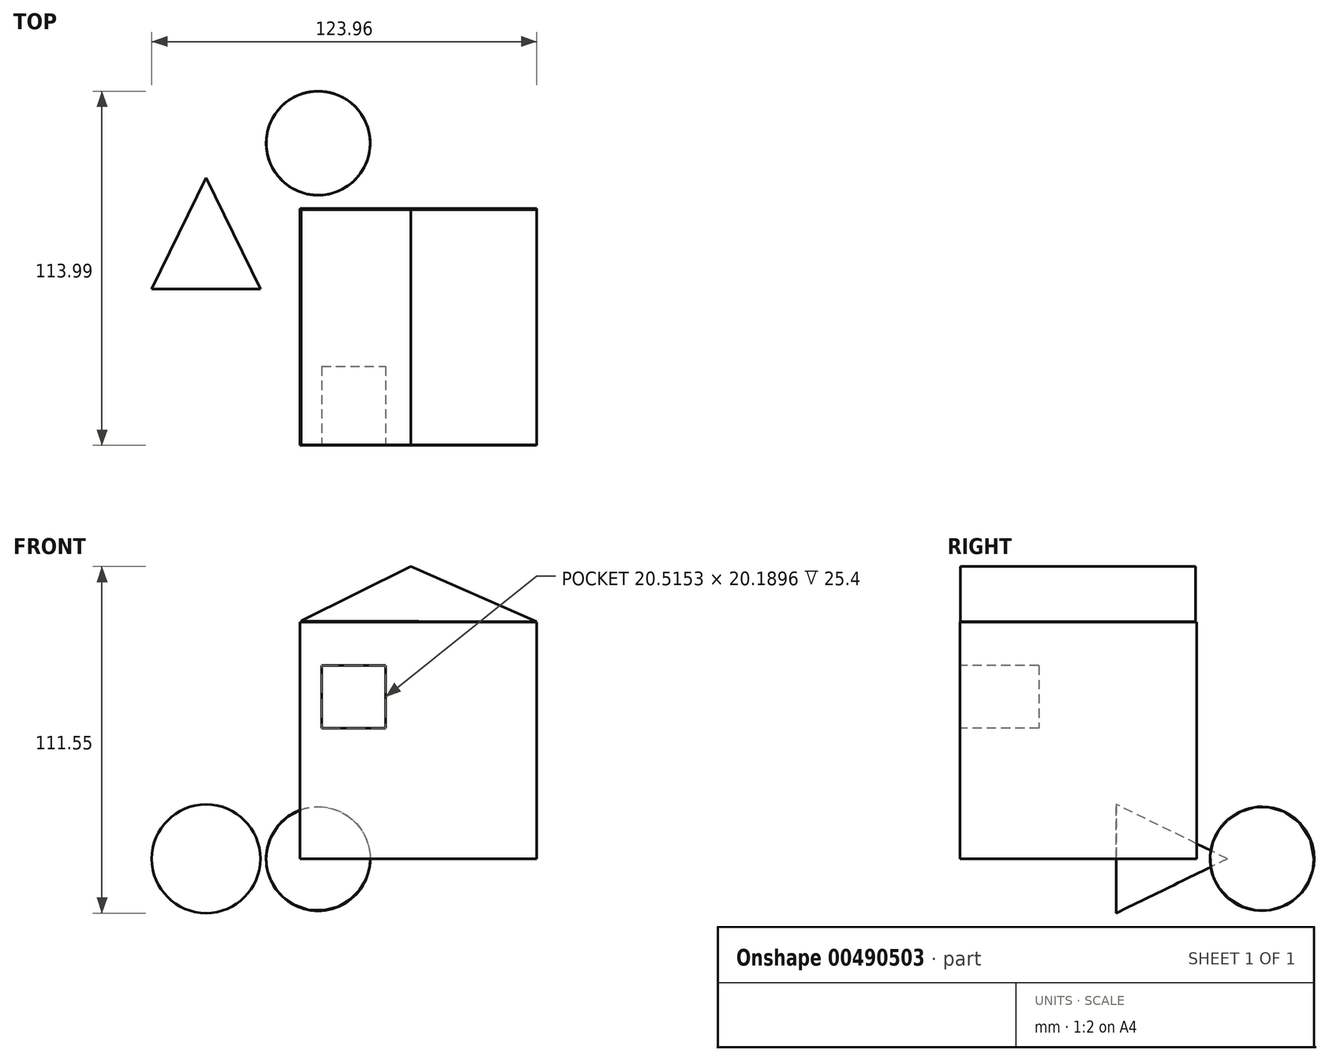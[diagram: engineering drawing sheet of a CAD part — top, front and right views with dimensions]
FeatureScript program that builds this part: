
annotation { "Feature Type Name" : "Feature", "Feature Type Description" : "" }
export const myFeature = defineFeature(function(context is Context, id is Id, definition is map)
    precondition{}
    {
        {
            var Q0;
            Q0=qCreatedBy(makeId("Top.planeOp"),FACE);
            var sketch = newSketch(context, id + "F0", { "sketchPlane" : qUnion([Q0])});
            skLineSegment(sketch, "E0.bottom", {"start": v(-35.62, 39.46) * mm, "end": v(40.58, 39.46) * mm});
            skLineSegment(sketch, "E0.top", {"start": v(-35.62, -36.74) * mm, "end": v(40.58, -36.74) * mm});
            skLineSegment(sketch, "E0.left", {"start": v(-35.62, 39.46) * mm, "end": v(-35.62, -36.74) * mm});
            skLineSegment(sketch, "E0.right", {"start": v(40.58, 39.46) * mm, "end": v(40.58, -36.74) * mm});
            skSolve(sketch);
        }
        {
            var Q0;
            Q0 = qSketchRegion(id + "F0", true);
            extrude(context, id + "F1", {"entities" : qUnion([Q0]), "depth" : 76.2 * mm});
        }
        {
            var Q0;
            Q0=qCreatedBy(makeId("Front.planeOp"),FACE);
            var sketch = newSketch(context, id + "F2", { "sketchPlane" : qUnion([Q0])});
            skLineSegment(sketch, "E1", {"start": v(-35.27, 76.57) * mm, "end": v(0, 94.06) * mm});
            skLineSegment(sketch, "E2", {"start": v(0, 94.06) * mm, "end": v(40.52, 76.28) * mm});
            skLineSegment(sketch, "E3", {"start": v(40.52, 76.28) * mm, "end": v(-35.27, 76.57) * mm});
            skSolve(sketch);
        }
        {
            var Q0;
            Q0=makeQuery(id+"F2.imprint","IMPRINT",FACE,{"disambiguationData":[TD([[makeQuery(id+"F2.imprint","IMPRINT",EDGE,{"derivedFrom":sQuery(id+"F2.wireOp",EDGE,"E1")}),-1.0]])]});
            extrude(context, id + "F3", {"entities" : qUnion([Q0]), "depth" : 36.58 * mm, "hasSecondDirection" : true, "secondDirectionOppositeDirection" : true, "secondDirectionDepth" : 39.12 * mm});
        }
        {
            var Q0;
            Q0=makeQuery(id+"F1.opExtrude","SWEPT_FACE",FACE,{"disambiguationData":[OSD([sQuery(id+"F0.wireOp",EDGE,"E0.top")])]});
            var sketch = newSketch(context, id + "F4", { "sketchPlane" : qUnion([Q0])});
            skLineSegment(sketch, "E4.bottom", {"start": v(-28.66, 62.17) * mm, "end": v(-8.14, 62.17) * mm});
            skLineSegment(sketch, "E4.top", {"start": v(-28.66, 41.98) * mm, "end": v(-8.14, 41.98) * mm});
            skLineSegment(sketch, "E4.left", {"start": v(-28.66, 62.17) * mm, "end": v(-28.66, 41.98) * mm});
            skLineSegment(sketch, "E4.right", {"start": v(-8.14, 62.17) * mm, "end": v(-8.14, 41.98) * mm});
            skSolve(sketch);
        }
        {
            var Q0;
            Q0 = qSketchRegion(id + "F4", true);
            extrude(context, id + "F5", {"entities" : qUnion([Q0]), "operationType" : NewBodyOperationType.REMOVE, "oppositeDirection" : true, "depth" : 25.4 * mm});
        }
        {
            var Q0;
            Q0=qCreatedBy(makeId("Top.planeOp"),FACE);
            var sketch = newSketch(context, id + "F6", { "sketchPlane" : qUnion([Q0])});
            skLineSegment(sketch, "E5", {"start": v(-65.9, 49.4) * mm, "end": v(-65.9, 13.55) * mm});
            skLineSegment(sketch, "E6", {"start": v(-65.9, 13.55) * mm, "end": v(-48.4, 13.55) * mm});
            skLineSegment(sketch, "E7", {"start": v(-48.4, 13.55) * mm, "end": v(-65.9, 49.4) * mm});
            skSolve(sketch);
        }
        {
            var Q0;
            Q0=makeQuery(id+"F6.imprint","IMPRINT",FACE,{"disambiguationData":[TD([[makeQuery(id+"F6.imprint","IMPRINT",EDGE,{"derivedFrom":sQuery(id+"F6.wireOp",EDGE,"E5")}),1.0]])]});
            var Q1;
            Q1=sQuery(id+"F6.wireOp",EDGE,"E5");
            revolve(context, id + "F7", {"entities" : qUnion([Q0]), "axis" : qUnion([Q1]), "revolveType" : RevolveType.ONE_DIRECTION, "oppositeDirection" : true, "angle" : 360 * degree});
        }
        {
            var Q0;
            Q0=qCreatedBy(makeId("Top.planeOp"),FACE);
            var sketch = newSketch(context, id + "F8", { "sketchPlane" : qUnion([Q0])});
            skCircle(sketch, "E8", {"center": v(-29.82, 60.48) * mm, "radius": 16.73 * mm});
            skPoint(sketch, "E8.first.point", {"position": v(-45.27, 66.9) * mm});
            skPoint(sketch, "E8.second.point", {"position": v(-16.12, 50.86) * mm});
            skPoint(sketch, "E8.third.point", {"position": v(-13.2, 58.44) * mm});
            skLineSegment(sketch, "E9", {"start": v(-45.27, 66.9) * mm, "end": v(-14.35, 54.1) * mm});
            skSolve(sketch);
        }
        {
            var Q0;
            {var subQ0=sQuery(id+"F8.wireOp",EDGE,"E9");Q0=makeQuery(id+"F8.imprint","IMPRINT",FACE,{"disambiguationData":[TD([[makeQuery(id+"F8.imprint","IMPRINT",EDGE,{"derivedFrom":subQ0}),1.0]])]});}
            var Q1;
            Q1=sQuery(id+"F8.wireOp",EDGE,"E9");
            revolve(context, id + "F9", {"entities" : qUnion([Q0]), "axis" : qUnion([Q1]), "revolveType" : RevolveType.FULL});
        }
    });
